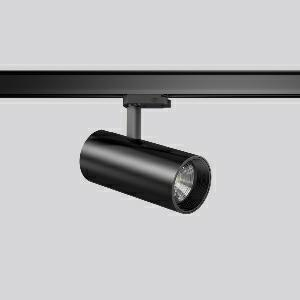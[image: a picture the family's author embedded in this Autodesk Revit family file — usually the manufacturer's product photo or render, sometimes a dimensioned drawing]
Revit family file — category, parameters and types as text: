
# Revit family: deecos_s_mini_742201_003_3_76_6adc
name_source: partatom
category: Lighting Fixtures
units: mm (PartAtom-declared; Revit-internal decimal feet)

## family parameters
Cut with Voids When Loaded = No
Host = Face
Light Source = No
Part Type = Normal
Room Calculation Point = No
Round Connector Dimension = Use Diameter
Shared = No

## types (1)
- DEECOS S mini (1 x LED Modul 935, 2300 lm, 3500)
    Apparent Load = 20 VA
    Approval mark = CE
    CIE Flux Codes = 80 99 100 100 100
    Color Rendering = 92
    Color Temperature = 3500
    Default Elevation = 1800 mm
    Description = Series: DEECOS S mini
LED surface-mounted projector in modern design with no visible cooling ribs. Housing: die-cast aluminium, powder-coated. Rotation range: 356°. Swivel range: 90°. Black plastic ring and recessed LED to prevent glare from the side. Optical assembly with lens made of plastic (polycarbonate) for the best homogeneous light distribution - can be changed without tools. Best colour rendering index Ra>90. With adapter for RZB 3-circuit DALI tracks. Suitable for Track on ceiling, Wall track. High quality converter without flickering and stroboscopic effect. The following accessories can be mounted without use of tools: interchangeable lenses, decorative glasses, honeycomb louvre, clear and frosted diffusers, white interchangeable plastic ring. 
Colour: deep black, matt (RAL 9005)
Diameter: 87 mm
Height: 214 mm
Lamp: LED
Socket: without socket
Colour temperature: 3500K
Colour rendering index (CRI): 92
System power: 20 W
Rated luminous flux: 2300 lm
Luminous efficiency: 115 lm/W
Control gear: Converter, dimmable, DALI
Protection class: I
Type of protection: IP 20
    Height = 214 mm
    Lamp = 1 x LED Modul 935
    Lamp Light Flux = 2300 lm
    Lamp count = 1
    Length = 87 mm
    Lifetime = 50000 h
    Luminous efficacy = 115 lm/W
    Manufacturer = RZB
    ModVariant = No
    Model = 742201.003.3.76
    Mounting Place = Ceiling
    Mounting Type = Rail mounted
    Number of Poles = 1
    OnlyDefault = Yes
    Power Factor = 1
    Product Name = DEECOS S mini
    Product group = Track mounted projectors
    ProductGroupID = 301
    Protection Class = Protection class I
    Protection Degree = IP 20
    RLX_Detail_Level = 1
    RLX_Emergency_Light_Flux = 0 lm
    RLX_Emergency_Type = 0
    RLX_Emergency_Type_DB = No
    RlxData = <blob elided: 38617 chars, md5=7d37939e>
    Socket = socket
    Standby Power = 0 W
    System Light Flux = 2300 lm
    System Power = 20 W
    Type Comments = Product without accessories
    Type Image = 741930.003.jpg
    URL = http://relux.com
    VarID = ---
    Voltage = 230 V
    Voltage Range = 220-240 V
    Weight = 0.00 kg
    Width = 0 mm  [stored 0 ft]

note: [stored X ft] marks values corroborated as IEEE doubles in the binary element streams (Revit-internal decimal feet)

## geometry (parser evidence)
native form markers: Blend x4, Sweep x11
no freeform markers — native parametric forms only
